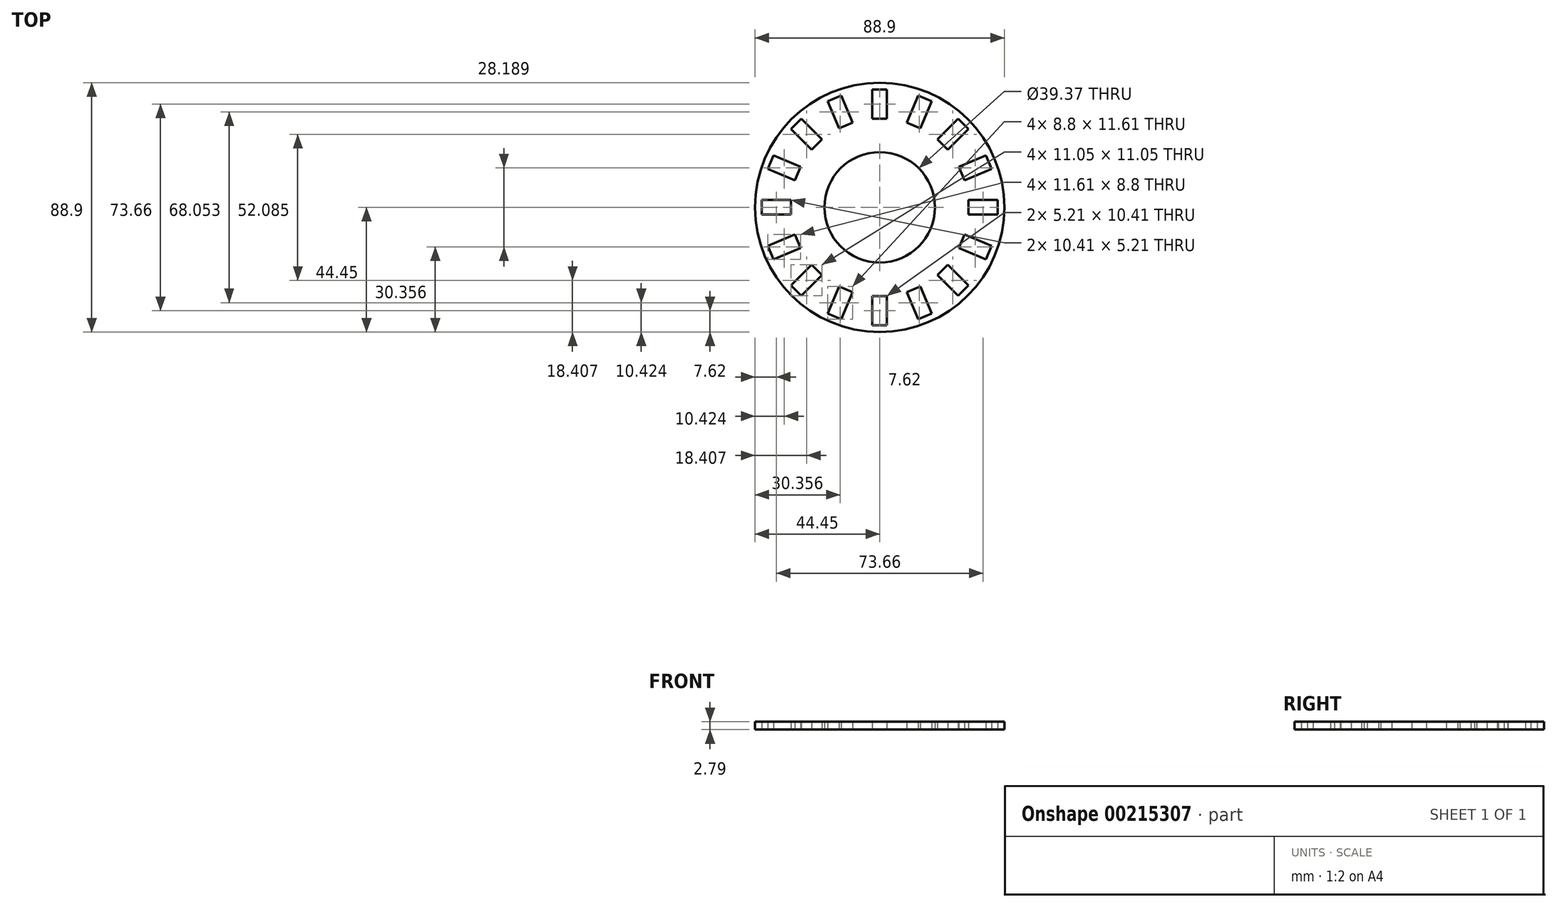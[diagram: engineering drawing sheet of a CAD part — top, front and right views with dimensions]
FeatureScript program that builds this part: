
annotation { "Feature Type Name" : "Feature", "Feature Type Description" : "" }
export const myFeature = defineFeature(function(context is Context, id is Id, definition is map)
    precondition{}
    {
        {
            var Q0;
            Q0=qCreatedBy(makeId("Top.planeOp"),FACE);
            var sketch = newSketch(context, id + "F0", { "sketchPlane" : qUnion([Q0])});
            skLineSegment(sketch, "E0.bottom", {"start": v(2.6, 31.62) * mm, "end": v(-2.6, 31.62) * mm});
            skLineSegment(sketch, "E0.top", {"start": v(2.6, 42.04) * mm, "end": v(-2.6, 42.04) * mm});
            skLineSegment(sketch, "E0.left", {"start": v(2.6, 31.62) * mm, "end": v(2.6, 42.04) * mm});
            skLineSegment(sketch, "E0.right", {"start": v(-2.6, 31.62) * mm, "end": v(-2.6, 42.04) * mm});
            skPoint(sketch, "E0.middle", {"position": v(0, 36.83) * mm});
            skLineSegment(sketch, "E1.1.0", {"start": v(-14.5, 28.22) * mm, "end": v(-18.5, 37.84) * mm});
            skLineSegment(sketch, "E1.1.1", {"start": v(-9.7, 30.21) * mm, "end": v(-13.68, 39.83) * mm});
            skLineSegment(sketch, "E1.1.2", {"start": v(-13.68, 39.83) * mm, "end": v(-18.5, 37.84) * mm});
            skLineSegment(sketch, "E1.1.3", {"start": v(-9.7, 30.21) * mm, "end": v(-14.5, 28.22) * mm});
            skPoint(sketch, "E1.1.4", {"position": v(-14.1, 34.03) * mm});
            skPoint(sketch, "E1.1.5", {"position": v(-14.1, 34.03) * mm});
            skPoint(sketch, "E1.1.6", {"position": v(-14.1, 34.03) * mm});
            skPoint(sketch, "E1.1.7", {"position": v(-14.1, 34.03) * mm});
            skPoint(sketch, "E1.1.8", {"position": v(-14.1, 34.03) * mm});
            skPoint(sketch, "E1.1.9", {"position": v(-14.1, 34.03) * mm});
            skPoint(sketch, "E1.1.10", {"position": v(-14.1, 34.03) * mm});
            skPoint(sketch, "E1.1.11", {"position": v(-14.1, 34.03) * mm});
            skPoint(sketch, "E1.1.12", {"position": v(-14.1, 34.03) * mm});
            skLineSegment(sketch, "E1.2.0", {"start": v(-24.2, 20.52) * mm, "end": v(-31.57, 27.88) * mm});
            skLineSegment(sketch, "E1.2.1", {"start": v(-20.52, 24.2) * mm, "end": v(-27.88, 31.57) * mm});
            skLineSegment(sketch, "E1.2.2", {"start": v(-27.88, 31.57) * mm, "end": v(-31.57, 27.88) * mm});
            skLineSegment(sketch, "E1.2.3", {"start": v(-20.52, 24.2) * mm, "end": v(-24.2, 20.52) * mm});
            skPoint(sketch, "E1.2.4", {"position": v(-26.04, 26.04) * mm});
            skPoint(sketch, "E1.2.5", {"position": v(-26.04, 26.04) * mm});
            skPoint(sketch, "E1.2.6", {"position": v(-26.04, 26.04) * mm});
            skPoint(sketch, "E1.2.7", {"position": v(-26.04, 26.04) * mm});
            skPoint(sketch, "E1.2.8", {"position": v(-26.04, 26.04) * mm});
            skPoint(sketch, "E1.2.9", {"position": v(-26.04, 26.04) * mm});
            skPoint(sketch, "E1.2.10", {"position": v(-26.04, 26.04) * mm});
            skPoint(sketch, "E1.2.11", {"position": v(-26.04, 26.04) * mm});
            skPoint(sketch, "E1.2.12", {"position": v(-26.04, 26.04) * mm});
            skLineSegment(sketch, "E1.3.0", {"start": v(-30.21, 9.7) * mm, "end": v(-39.83, 13.68) * mm});
            skLineSegment(sketch, "E1.3.1", {"start": v(-28.22, 14.5) * mm, "end": v(-37.84, 18.5) * mm});
            skLineSegment(sketch, "E1.3.2", {"start": v(-37.84, 18.5) * mm, "end": v(-39.83, 13.68) * mm});
            skLineSegment(sketch, "E1.3.3", {"start": v(-28.22, 14.5) * mm, "end": v(-30.21, 9.7) * mm});
            skPoint(sketch, "E1.3.4", {"position": v(-34.03, 14.1) * mm});
            skPoint(sketch, "E1.3.5", {"position": v(-34.03, 14.1) * mm});
            skPoint(sketch, "E1.3.6", {"position": v(-34.03, 14.1) * mm});
            skPoint(sketch, "E1.3.7", {"position": v(-34.03, 14.1) * mm});
            skPoint(sketch, "E1.3.8", {"position": v(-34.03, 14.1) * mm});
            skPoint(sketch, "E1.3.9", {"position": v(-34.03, 14.1) * mm});
            skPoint(sketch, "E1.3.10", {"position": v(-34.03, 14.1) * mm});
            skPoint(sketch, "E1.3.11", {"position": v(-34.03, 14.1) * mm});
            skPoint(sketch, "E1.3.12", {"position": v(-34.03, 14.1) * mm});
            skLineSegment(sketch, "E1.4.0", {"start": v(-31.62, -2.6) * mm, "end": v(-42.04, -2.6) * mm});
            skLineSegment(sketch, "E1.4.1", {"start": v(-31.62, 2.6) * mm, "end": v(-42.04, 2.6) * mm});
            skLineSegment(sketch, "E1.4.2", {"start": v(-42.04, 2.6) * mm, "end": v(-42.04, -2.6) * mm});
            skLineSegment(sketch, "E1.4.3", {"start": v(-31.62, 2.6) * mm, "end": v(-31.62, -2.6) * mm});
            skPoint(sketch, "E1.4.4", {"position": v(-36.83, 0) * mm});
            skPoint(sketch, "E1.4.5", {"position": v(-36.83, 0) * mm});
            skPoint(sketch, "E1.4.6", {"position": v(-36.83, 0) * mm});
            skPoint(sketch, "E1.4.7", {"position": v(-36.83, 0) * mm});
            skPoint(sketch, "E1.4.8", {"position": v(-36.83, 0) * mm});
            skPoint(sketch, "E1.4.9", {"position": v(-36.83, 0) * mm});
            skPoint(sketch, "E1.4.10", {"position": v(-36.83, 0) * mm});
            skPoint(sketch, "E1.4.11", {"position": v(-36.83, 0) * mm});
            skPoint(sketch, "E1.4.12", {"position": v(-36.83, 0) * mm});
            skLineSegment(sketch, "E1.5.0", {"start": v(-28.22, -14.5) * mm, "end": v(-37.84, -18.5) * mm});
            skLineSegment(sketch, "E1.5.1", {"start": v(-30.21, -9.7) * mm, "end": v(-39.83, -13.68) * mm});
            skLineSegment(sketch, "E1.5.2", {"start": v(-39.83, -13.68) * mm, "end": v(-37.84, -18.5) * mm});
            skLineSegment(sketch, "E1.5.3", {"start": v(-30.21, -9.7) * mm, "end": v(-28.22, -14.5) * mm});
            skPoint(sketch, "E1.5.4", {"position": v(-34.03, -14.1) * mm});
            skPoint(sketch, "E1.5.5", {"position": v(-34.03, -14.1) * mm});
            skPoint(sketch, "E1.5.6", {"position": v(-34.03, -14.1) * mm});
            skPoint(sketch, "E1.5.7", {"position": v(-34.03, -14.1) * mm});
            skPoint(sketch, "E1.5.8", {"position": v(-34.03, -14.1) * mm});
            skPoint(sketch, "E1.5.9", {"position": v(-34.03, -14.1) * mm});
            skPoint(sketch, "E1.5.10", {"position": v(-34.03, -14.1) * mm});
            skPoint(sketch, "E1.5.11", {"position": v(-34.03, -14.1) * mm});
            skPoint(sketch, "E1.5.12", {"position": v(-34.03, -14.1) * mm});
            skLineSegment(sketch, "E1.6.0", {"start": v(-20.52, -24.2) * mm, "end": v(-27.88, -31.57) * mm});
            skLineSegment(sketch, "E1.6.1", {"start": v(-24.2, -20.52) * mm, "end": v(-31.57, -27.88) * mm});
            skLineSegment(sketch, "E1.6.2", {"start": v(-31.57, -27.88) * mm, "end": v(-27.88, -31.57) * mm});
            skLineSegment(sketch, "E1.6.3", {"start": v(-24.2, -20.52) * mm, "end": v(-20.52, -24.2) * mm});
            skPoint(sketch, "E1.6.4", {"position": v(-26.04, -26.04) * mm});
            skPoint(sketch, "E1.6.5", {"position": v(-26.04, -26.04) * mm});
            skPoint(sketch, "E1.6.6", {"position": v(-26.04, -26.04) * mm});
            skPoint(sketch, "E1.6.7", {"position": v(-26.04, -26.04) * mm});
            skPoint(sketch, "E1.6.8", {"position": v(-26.04, -26.04) * mm});
            skPoint(sketch, "E1.6.9", {"position": v(-26.04, -26.04) * mm});
            skPoint(sketch, "E1.6.10", {"position": v(-26.04, -26.04) * mm});
            skPoint(sketch, "E1.6.11", {"position": v(-26.04, -26.04) * mm});
            skPoint(sketch, "E1.6.12", {"position": v(-26.04, -26.04) * mm});
            skLineSegment(sketch, "E1.7.0", {"start": v(-9.7, -30.21) * mm, "end": v(-13.68, -39.83) * mm});
            skLineSegment(sketch, "E1.7.1", {"start": v(-14.5, -28.22) * mm, "end": v(-18.5, -37.84) * mm});
            skLineSegment(sketch, "E1.7.2", {"start": v(-18.5, -37.84) * mm, "end": v(-13.68, -39.83) * mm});
            skLineSegment(sketch, "E1.7.3", {"start": v(-14.5, -28.22) * mm, "end": v(-9.7, -30.21) * mm});
            skPoint(sketch, "E1.7.4", {"position": v(-14.1, -34.03) * mm});
            skPoint(sketch, "E1.7.5", {"position": v(-14.1, -34.03) * mm});
            skPoint(sketch, "E1.7.6", {"position": v(-14.1, -34.03) * mm});
            skPoint(sketch, "E1.7.7", {"position": v(-14.1, -34.03) * mm});
            skPoint(sketch, "E1.7.8", {"position": v(-14.1, -34.03) * mm});
            skPoint(sketch, "E1.7.9", {"position": v(-14.1, -34.03) * mm});
            skPoint(sketch, "E1.7.10", {"position": v(-14.1, -34.03) * mm});
            skPoint(sketch, "E1.7.11", {"position": v(-14.1, -34.03) * mm});
            skPoint(sketch, "E1.7.12", {"position": v(-14.1, -34.03) * mm});
            skLineSegment(sketch, "E1.8.0", {"start": v(2.6, -31.62) * mm, "end": v(2.6, -42.04) * mm});
            skLineSegment(sketch, "E1.8.1", {"start": v(-2.6, -31.62) * mm, "end": v(-2.6, -42.04) * mm});
            skLineSegment(sketch, "E1.8.2", {"start": v(-2.6, -42.04) * mm, "end": v(2.6, -42.04) * mm});
            skLineSegment(sketch, "E1.8.3", {"start": v(-2.6, -31.62) * mm, "end": v(2.6, -31.62) * mm});
            skPoint(sketch, "E1.8.4", {"position": v(0, -36.83) * mm});
            skPoint(sketch, "E1.8.5", {"position": v(0, -36.83) * mm});
            skPoint(sketch, "E1.8.6", {"position": v(0, -36.83) * mm});
            skPoint(sketch, "E1.8.7", {"position": v(0, -36.83) * mm});
            skPoint(sketch, "E1.8.8", {"position": v(0, -36.83) * mm});
            skPoint(sketch, "E1.8.9", {"position": v(0, -36.83) * mm});
            skPoint(sketch, "E1.8.10", {"position": v(0, -36.83) * mm});
            skPoint(sketch, "E1.8.11", {"position": v(0, -36.83) * mm});
            skPoint(sketch, "E1.8.12", {"position": v(0, -36.83) * mm});
            skLineSegment(sketch, "E1.9.0", {"start": v(14.5, -28.22) * mm, "end": v(18.5, -37.84) * mm});
            skLineSegment(sketch, "E1.9.1", {"start": v(9.7, -30.21) * mm, "end": v(13.68, -39.83) * mm});
            skLineSegment(sketch, "E1.9.2", {"start": v(13.68, -39.83) * mm, "end": v(18.5, -37.84) * mm});
            skLineSegment(sketch, "E1.9.3", {"start": v(9.7, -30.21) * mm, "end": v(14.5, -28.22) * mm});
            skPoint(sketch, "E1.9.4", {"position": v(14.1, -34.03) * mm});
            skPoint(sketch, "E1.9.5", {"position": v(14.1, -34.03) * mm});
            skPoint(sketch, "E1.9.6", {"position": v(14.1, -34.03) * mm});
            skPoint(sketch, "E1.9.7", {"position": v(14.1, -34.03) * mm});
            skPoint(sketch, "E1.9.8", {"position": v(14.1, -34.03) * mm});
            skPoint(sketch, "E1.9.9", {"position": v(14.1, -34.03) * mm});
            skPoint(sketch, "E1.9.10", {"position": v(14.1, -34.03) * mm});
            skPoint(sketch, "E1.9.11", {"position": v(14.1, -34.03) * mm});
            skPoint(sketch, "E1.9.12", {"position": v(14.1, -34.03) * mm});
            skLineSegment(sketch, "E1.10.0", {"start": v(24.2, -20.52) * mm, "end": v(31.57, -27.88) * mm});
            skLineSegment(sketch, "E1.10.1", {"start": v(20.52, -24.2) * mm, "end": v(27.88, -31.57) * mm});
            skLineSegment(sketch, "E1.10.2", {"start": v(27.88, -31.57) * mm, "end": v(31.57, -27.88) * mm});
            skLineSegment(sketch, "E1.10.3", {"start": v(20.52, -24.2) * mm, "end": v(24.2, -20.52) * mm});
            skPoint(sketch, "E1.10.4", {"position": v(26.04, -26.04) * mm});
            skPoint(sketch, "E1.10.5", {"position": v(26.04, -26.04) * mm});
            skPoint(sketch, "E1.10.6", {"position": v(26.04, -26.04) * mm});
            skPoint(sketch, "E1.10.7", {"position": v(26.04, -26.04) * mm});
            skPoint(sketch, "E1.10.8", {"position": v(26.04, -26.04) * mm});
            skPoint(sketch, "E1.10.9", {"position": v(26.04, -26.04) * mm});
            skPoint(sketch, "E1.10.10", {"position": v(26.04, -26.04) * mm});
            skPoint(sketch, "E1.10.11", {"position": v(26.04, -26.04) * mm});
            skPoint(sketch, "E1.10.12", {"position": v(26.04, -26.04) * mm});
            skLineSegment(sketch, "E1.11.0", {"start": v(30.21, -9.7) * mm, "end": v(39.83, -13.68) * mm});
            skLineSegment(sketch, "E1.11.1", {"start": v(28.22, -14.5) * mm, "end": v(37.84, -18.5) * mm});
            skLineSegment(sketch, "E1.11.2", {"start": v(37.84, -18.5) * mm, "end": v(39.83, -13.68) * mm});
            skLineSegment(sketch, "E1.11.3", {"start": v(28.22, -14.5) * mm, "end": v(30.21, -9.7) * mm});
            skPoint(sketch, "E1.11.4", {"position": v(34.03, -14.1) * mm});
            skPoint(sketch, "E1.11.5", {"position": v(34.03, -14.1) * mm});
            skPoint(sketch, "E1.11.6", {"position": v(34.03, -14.1) * mm});
            skPoint(sketch, "E1.11.7", {"position": v(34.03, -14.1) * mm});
            skPoint(sketch, "E1.11.8", {"position": v(34.03, -14.1) * mm});
            skPoint(sketch, "E1.11.9", {"position": v(34.03, -14.1) * mm});
            skPoint(sketch, "E1.11.10", {"position": v(34.03, -14.1) * mm});
            skPoint(sketch, "E1.11.11", {"position": v(34.03, -14.1) * mm});
            skPoint(sketch, "E1.11.12", {"position": v(34.03, -14.1) * mm});
            skLineSegment(sketch, "E1.12.0", {"start": v(31.62, 2.6) * mm, "end": v(42.04, 2.6) * mm});
            skLineSegment(sketch, "E1.12.1", {"start": v(31.62, -2.6) * mm, "end": v(42.04, -2.6) * mm});
            skLineSegment(sketch, "E1.12.2", {"start": v(42.04, -2.6) * mm, "end": v(42.04, 2.6) * mm});
            skLineSegment(sketch, "E1.12.3", {"start": v(31.62, -2.6) * mm, "end": v(31.62, 2.6) * mm});
            skPoint(sketch, "E1.12.4", {"position": v(36.83, 0) * mm});
            skPoint(sketch, "E1.12.5", {"position": v(36.83, 0) * mm});
            skPoint(sketch, "E1.12.6", {"position": v(36.83, 0) * mm});
            skPoint(sketch, "E1.12.7", {"position": v(36.83, 0) * mm});
            skPoint(sketch, "E1.12.8", {"position": v(36.83, 0) * mm});
            skPoint(sketch, "E1.12.9", {"position": v(36.83, 0) * mm});
            skPoint(sketch, "E1.12.10", {"position": v(36.83, 0) * mm});
            skPoint(sketch, "E1.12.11", {"position": v(36.83, 0) * mm});
            skPoint(sketch, "E1.12.12", {"position": v(36.83, 0) * mm});
            skLineSegment(sketch, "E1.13.0", {"start": v(28.22, 14.5) * mm, "end": v(37.84, 18.5) * mm});
            skLineSegment(sketch, "E1.13.1", {"start": v(30.21, 9.7) * mm, "end": v(39.83, 13.68) * mm});
            skLineSegment(sketch, "E1.13.2", {"start": v(39.83, 13.68) * mm, "end": v(37.84, 18.5) * mm});
            skLineSegment(sketch, "E1.13.3", {"start": v(30.21, 9.7) * mm, "end": v(28.22, 14.5) * mm});
            skPoint(sketch, "E1.13.4", {"position": v(34.03, 14.1) * mm});
            skPoint(sketch, "E1.13.5", {"position": v(34.03, 14.1) * mm});
            skPoint(sketch, "E1.13.6", {"position": v(34.03, 14.1) * mm});
            skPoint(sketch, "E1.13.7", {"position": v(34.03, 14.1) * mm});
            skPoint(sketch, "E1.13.8", {"position": v(34.03, 14.1) * mm});
            skPoint(sketch, "E1.13.9", {"position": v(34.03, 14.1) * mm});
            skPoint(sketch, "E1.13.10", {"position": v(34.03, 14.1) * mm});
            skPoint(sketch, "E1.13.11", {"position": v(34.03, 14.1) * mm});
            skPoint(sketch, "E1.13.12", {"position": v(34.03, 14.1) * mm});
            skLineSegment(sketch, "E1.14.0", {"start": v(20.52, 24.2) * mm, "end": v(27.88, 31.57) * mm});
            skLineSegment(sketch, "E1.14.1", {"start": v(24.2, 20.52) * mm, "end": v(31.57, 27.88) * mm});
            skLineSegment(sketch, "E1.14.2", {"start": v(31.57, 27.88) * mm, "end": v(27.88, 31.57) * mm});
            skLineSegment(sketch, "E1.14.3", {"start": v(24.2, 20.52) * mm, "end": v(20.52, 24.2) * mm});
            skPoint(sketch, "E1.14.4", {"position": v(26.04, 26.04) * mm});
            skPoint(sketch, "E1.14.5", {"position": v(26.04, 26.04) * mm});
            skPoint(sketch, "E1.14.6", {"position": v(26.04, 26.04) * mm});
            skPoint(sketch, "E1.14.7", {"position": v(26.04, 26.04) * mm});
            skPoint(sketch, "E1.14.8", {"position": v(26.04, 26.04) * mm});
            skPoint(sketch, "E1.14.9", {"position": v(26.04, 26.04) * mm});
            skPoint(sketch, "E1.14.10", {"position": v(26.04, 26.04) * mm});
            skPoint(sketch, "E1.14.11", {"position": v(26.04, 26.04) * mm});
            skPoint(sketch, "E1.14.12", {"position": v(26.04, 26.04) * mm});
            skLineSegment(sketch, "E1.15.0", {"start": v(9.7, 30.21) * mm, "end": v(13.68, 39.83) * mm});
            skLineSegment(sketch, "E1.15.1", {"start": v(14.5, 28.22) * mm, "end": v(18.5, 37.84) * mm});
            skLineSegment(sketch, "E1.15.2", {"start": v(18.5, 37.84) * mm, "end": v(13.68, 39.83) * mm});
            skLineSegment(sketch, "E1.15.3", {"start": v(14.5, 28.22) * mm, "end": v(9.7, 30.21) * mm});
            skPoint(sketch, "E1.15.4", {"position": v(14.1, 34.03) * mm});
            skPoint(sketch, "E1.15.5", {"position": v(14.1, 34.03) * mm});
            skPoint(sketch, "E1.15.6", {"position": v(14.1, 34.03) * mm});
            skPoint(sketch, "E1.15.7", {"position": v(14.1, 34.03) * mm});
            skPoint(sketch, "E1.15.8", {"position": v(14.1, 34.03) * mm});
            skPoint(sketch, "E1.15.9", {"position": v(14.1, 34.03) * mm});
            skPoint(sketch, "E1.15.10", {"position": v(14.1, 34.03) * mm});
            skPoint(sketch, "E1.15.11", {"position": v(14.1, 34.03) * mm});
            skPoint(sketch, "E1.15.12", {"position": v(14.1, 34.03) * mm});
            skPoint(sketch, "E1.center", {"position": v(0, 0) * mm});
            skCircle(sketch, "E2", {"center": v(0, 0) * mm, "radius": 19.69 * mm});
            skCircle(sketch, "E3", {"center": v(0, 0) * mm, "radius": 44.45 * mm});
            skPoint(sketch, "E4", {"position": v(0, 42.04) * mm});
            skPoint(sketch, "E5", {"position": v(0, 44.45) * mm});
            skSolve(sketch);
        }
        {
            var Q0;
            Q0=makeQuery(id+"F0.imprint","IMPRINT",FACE,{"disambiguationData":[TD([[makeQuery(id+"F0.imprint","IMPRINT",EDGE,{"derivedFrom":sQuery(id+"F0.wireOp",EDGE,"E0.bottom")}),1.0]])]});
            extrude(context, id + "F1", {"entities" : qUnion([Q0]), "depth" : 2.8 * mm});
        }
    });
